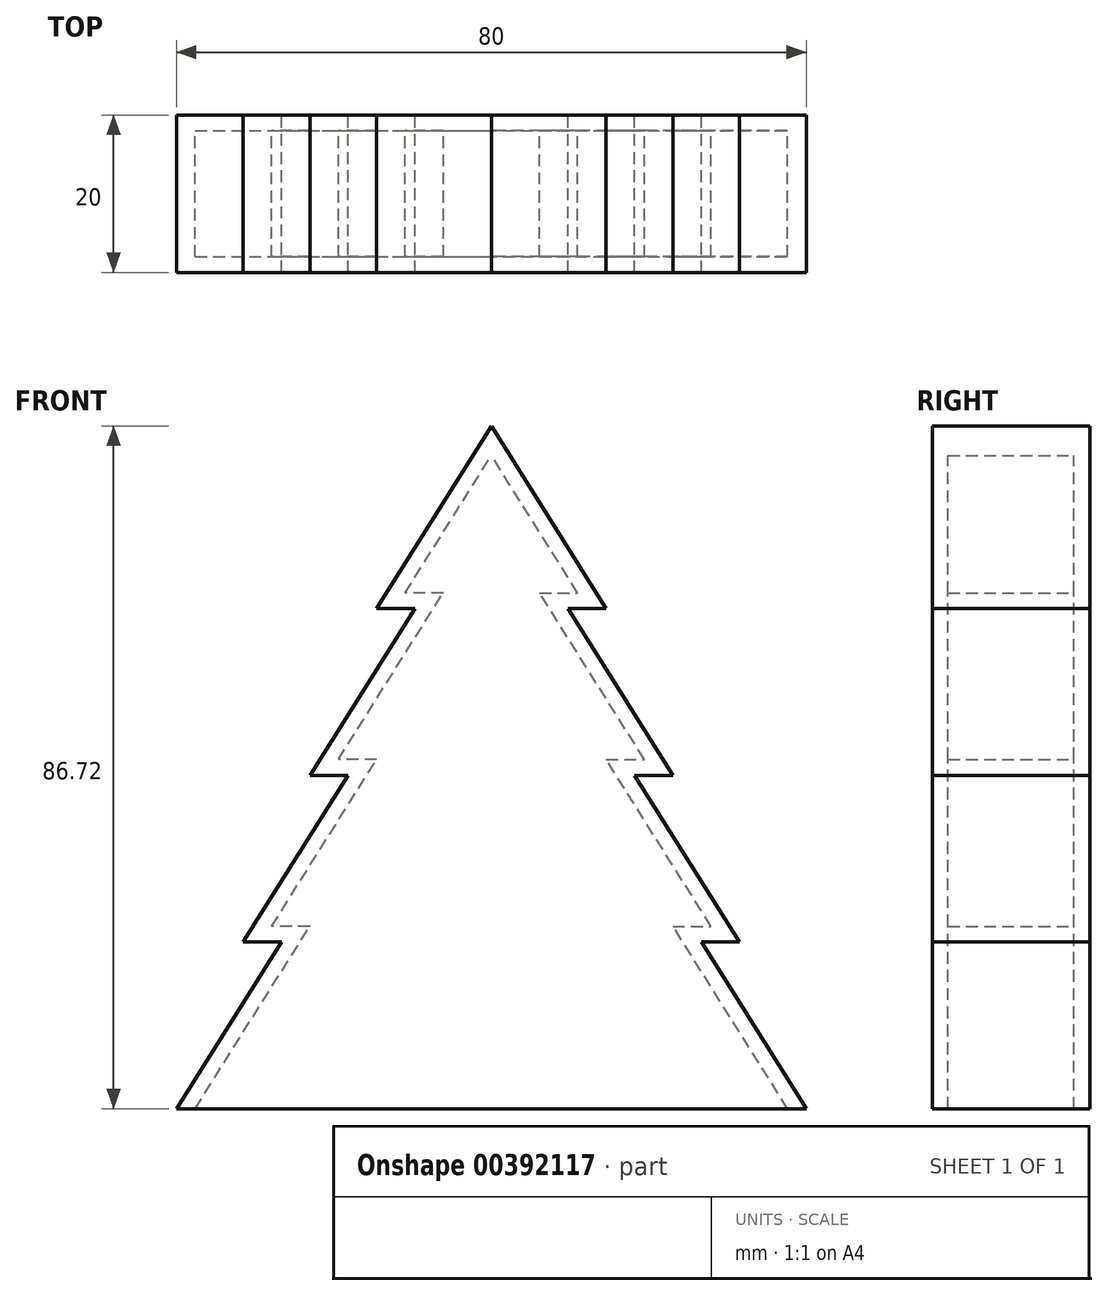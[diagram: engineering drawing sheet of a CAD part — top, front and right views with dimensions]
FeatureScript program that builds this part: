
annotation { "Feature Type Name" : "Feature", "Feature Type Description" : "" }
export const myFeature = defineFeature(function(context is Context, id is Id, definition is map)
    precondition{}
    {
        {
            var Q0;
            Q0=qCreatedBy(makeId("Front.planeOp"),FACE);
            var sketch = newSketch(context, id + "F0", { "sketchPlane" : qUnion([Q0])});
            skLineSegment(sketch, "E0", {"start": v(0, 100) * mm, "end": v(0, 0) * mm, "construction": true});
            skLineSegment(sketch, "E1", {"start": v(0, 0) * mm, "end": v(40, 0) * mm});
            skLineSegment(sketch, "E2", {"start": v(0, 100) * mm, "end": v(40, 0) * mm, "construction": true});
            skLineSegment(sketch, "E3", {"start": v(40, 0) * mm, "end": v(26.67, 21.18) * mm});
            skLineSegment(sketch, "E4", {"start": v(26.67, 21.18) * mm, "end": v(31.53, 21.18) * mm});
            skLineSegment(sketch, "E5", {"start": v(31.53, 21.18) * mm, "end": v(18.2, 42.36) * mm});
            skLineSegment(sketch, "E6", {"start": v(18.2, 42.36) * mm, "end": v(23.06, 42.36) * mm});
            skLineSegment(sketch, "E7", {"start": v(23.06, 42.36) * mm, "end": v(9.73, 63.54) * mm});
            skLineSegment(sketch, "E8", {"start": v(9.73, 63.54) * mm, "end": v(14.58, 63.54) * mm});
            skLineSegment(sketch, "E9", {"start": v(14.58, 63.54) * mm, "end": v(0, 86.72) * mm});
            skLineSegment(sketch, "E10", {"start": v(0, 0) * mm, "end": v(0, 86.72) * mm});
            skSolve(sketch);
        }
        {
            var Q0;
            Q0 = qSketchRegion(id + "F0", true);
            extrude(context, id + "F1", {"entities" : qUnion([Q0]), "depth" : 20 * mm});
        }
        {
            var Q0;
            Q0=makeQuery(id+"F1.opExtrude","SWEPT_BODY",BODY,{"disambiguationData":[OSD([sQuery(id+"F0.wireOp",EDGE,"E1"),sQuery(id+"F0.wireOp",EDGE,"E3"),sQuery(id+"F0.wireOp",EDGE,"E4"),sQuery(id+"F0.wireOp",EDGE,"E5"),sQuery(id+"F0.wireOp",EDGE,"E6"),sQuery(id+"F0.wireOp",EDGE,"E7"),sQuery(id+"F0.wireOp",EDGE,"E8"),sQuery(id+"F0.wireOp",EDGE,"E9"),sQuery(id+"F0.wireOp",EDGE,"E10")])]});
            var Q1;
            Q1=qCreatedBy(makeId("Right.planeOp"),FACE);
            mirror(context, id + "F2", {"operationType" : NewBodyOperationType.ADD, "entities" : qUnion([Q0]), "mirrorPlane" : qUnion([Q1])});
        }
        {
            var Q0;
            {var subQ0=makeQuery(id+"F1.opExtrude","SWEPT_FACE",FACE,{"disambiguationData":[OSD([sQuery(id+"F0.wireOp",EDGE,"E1")])]});Q0=makeQuery(id+"F2.boolean.opBoolean","MERGE",FACE,{"derivedFrom":[subQ0,makeQuery(id+"F2.opPattern","COPY",FACE,{"derivedFrom":subQ0,"instanceName":"1"})]});}
            shell(context, id + "F3", {"entities" : qUnion([Q0]), "thickness" : 2 * mm});
        }
    });
